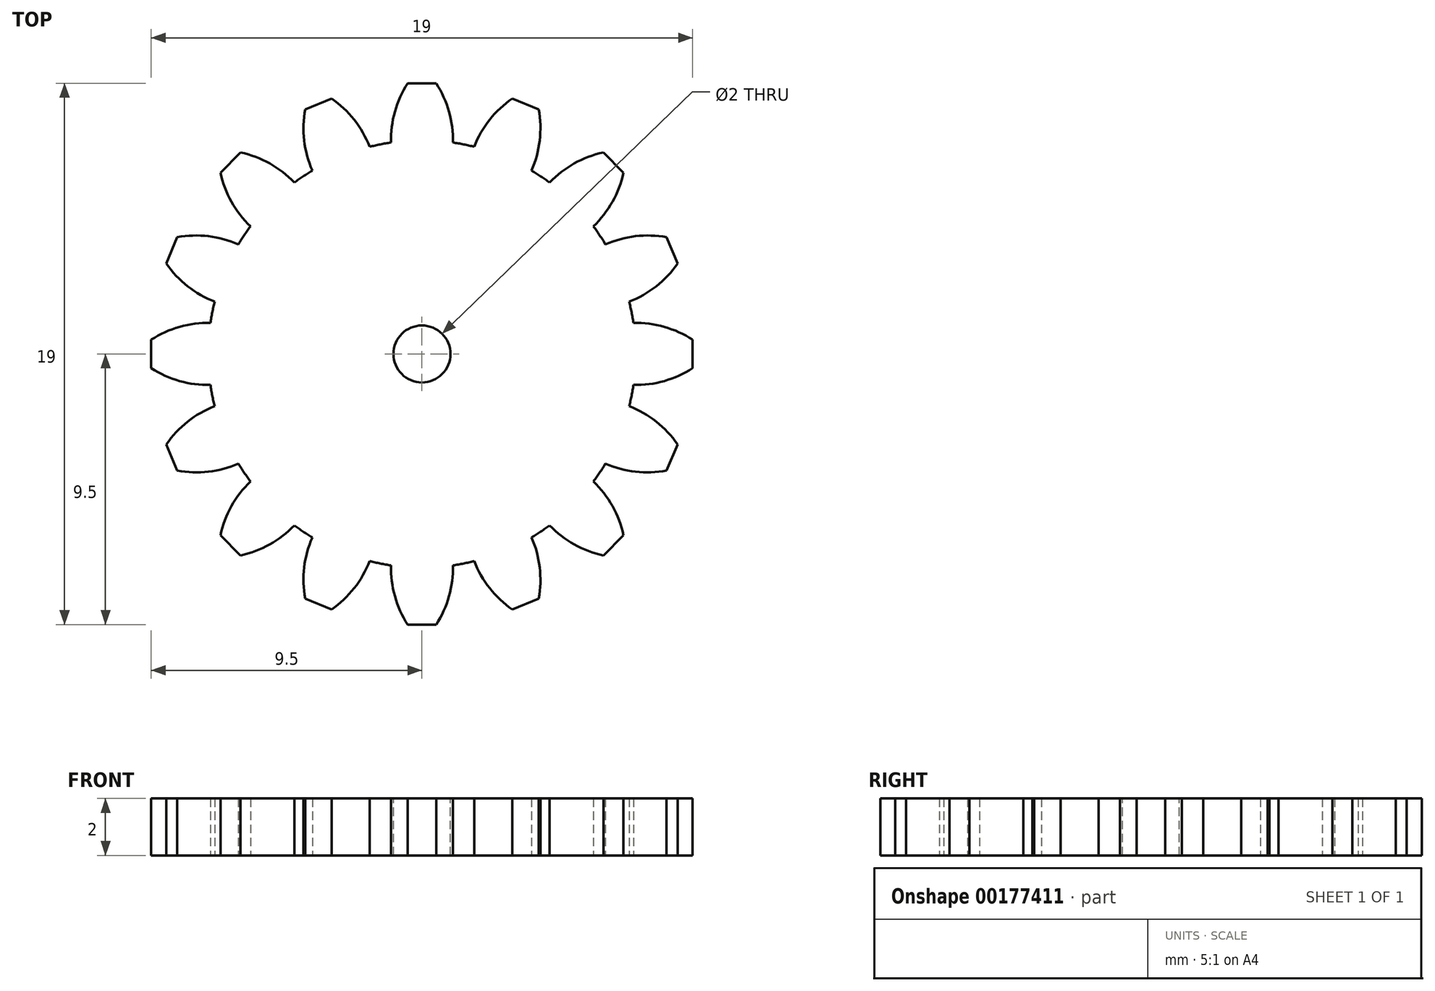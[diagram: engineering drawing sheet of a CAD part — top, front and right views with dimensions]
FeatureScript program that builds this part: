
annotation { "Feature Type Name" : "Feature", "Feature Type Description" : "" }
export const myFeature = defineFeature(function(context is Context, id is Id, definition is map)
    precondition{}
    {
        {
            var Q0;
            Q0=qCreatedBy(makeId("Top.planeOp"),FACE);
            var sketch = newSketch(context, id + "F0", { "sketchPlane" : qUnion([Q0])});
            skCircle(sketch, "E0", {"center": v(0, 0) * mm, "radius": 7.5 * mm});
            skLineSegment(sketch, "E1", {"start": v(0, 0) * mm, "end": v(0, 7.5) * mm, "construction": true});
            skLineSegment(sketch, "E2", {"start": v(0, 9.5) * mm, "end": v(-0.5, 9.5) * mm});
            skArc(sketch, "E3", {"start": v(-0.5, 9.5) * mm, "mid": v(-0.95, 8.5) * mm, "end": v(-1.09, 7.42) * mm});
            skLineSegment(sketch, "E4.MirrorCS", {"start": v(0, 9.5) * mm, "end": v(0.5, 9.5) * mm});
            skArc(sketch, "E5.MirrorCS", {"start": v(0.5, 9.5) * mm, "mid": v(0.95, 8.5) * mm, "end": v(1.09, 7.42) * mm});
            skArc(sketch, "E6.1.0", {"start": v(-4.1, 8.59) * mm, "mid": v(-4.13, 7.5) * mm, "end": v(-3.85, 6.44) * mm});
            skLineSegment(sketch, "E6.1.1", {"start": v(-3.64, 8.78) * mm, "end": v(-4.1, 8.59) * mm});
            skLineSegment(sketch, "E6.1.2", {"start": v(-3.64, 8.78) * mm, "end": v(-3.17, 8.97) * mm});
            skArc(sketch, "E6.1.3", {"start": v(-3.17, 8.97) * mm, "mid": v(-2.38, 8.22) * mm, "end": v(-1.83, 7.27) * mm});
            skArc(sketch, "E6.2.0", {"start": v(-7.07, 6.36) * mm, "mid": v(-6.69, 5.34) * mm, "end": v(-6.02, 4.48) * mm});
            skLineSegment(sketch, "E6.2.1", {"start": v(-6.72, 6.72) * mm, "end": v(-7.07, 6.36) * mm});
            skLineSegment(sketch, "E6.2.2", {"start": v(-6.72, 6.72) * mm, "end": v(-6.36, 7.07) * mm});
            skArc(sketch, "E6.2.3", {"start": v(-6.36, 7.07) * mm, "mid": v(-5.34, 6.69) * mm, "end": v(-4.48, 6.02) * mm});
            skArc(sketch, "E6.3.0", {"start": v(-8.97, 3.17) * mm, "mid": v(-8.22, 2.38) * mm, "end": v(-7.27, 1.83) * mm});
            skLineSegment(sketch, "E6.3.1", {"start": v(-8.78, 3.64) * mm, "end": v(-8.97, 3.17) * mm});
            skLineSegment(sketch, "E6.3.2", {"start": v(-8.78, 3.64) * mm, "end": v(-8.59, 4.1) * mm});
            skArc(sketch, "E6.3.3", {"start": v(-8.59, 4.1) * mm, "mid": v(-7.5, 4.13) * mm, "end": v(-6.44, 3.85) * mm});
            skArc(sketch, "E6.4.0", {"start": v(-9.5, -0.5) * mm, "mid": v(-8.5, -0.95) * mm, "end": v(-7.42, -1.09) * mm});
            skLineSegment(sketch, "E6.4.1", {"start": v(-9.5, 0) * mm, "end": v(-9.5, -0.5) * mm});
            skLineSegment(sketch, "E6.4.2", {"start": v(-9.5, 0) * mm, "end": v(-9.5, 0.5) * mm});
            skArc(sketch, "E6.4.3", {"start": v(-9.5, 0.5) * mm, "mid": v(-8.5, 0.95) * mm, "end": v(-7.42, 1.09) * mm});
            skArc(sketch, "E6.5.0", {"start": v(-8.59, -4.1) * mm, "mid": v(-7.5, -4.13) * mm, "end": v(-6.44, -3.85) * mm});
            skLineSegment(sketch, "E6.5.1", {"start": v(-8.78, -3.64) * mm, "end": v(-8.59, -4.1) * mm});
            skLineSegment(sketch, "E6.5.2", {"start": v(-8.78, -3.64) * mm, "end": v(-8.97, -3.17) * mm});
            skArc(sketch, "E6.5.3", {"start": v(-8.97, -3.17) * mm, "mid": v(-8.22, -2.38) * mm, "end": v(-7.27, -1.83) * mm});
            skArc(sketch, "E6.6.0", {"start": v(-6.36, -7.07) * mm, "mid": v(-5.34, -6.69) * mm, "end": v(-4.48, -6.02) * mm});
            skLineSegment(sketch, "E6.6.1", {"start": v(-6.72, -6.72) * mm, "end": v(-6.36, -7.07) * mm});
            skLineSegment(sketch, "E6.6.2", {"start": v(-6.72, -6.72) * mm, "end": v(-7.07, -6.36) * mm});
            skArc(sketch, "E6.6.3", {"start": v(-7.07, -6.36) * mm, "mid": v(-6.69, -5.34) * mm, "end": v(-6.02, -4.48) * mm});
            skArc(sketch, "E6.7.0", {"start": v(-3.17, -8.97) * mm, "mid": v(-2.38, -8.22) * mm, "end": v(-1.83, -7.27) * mm});
            skLineSegment(sketch, "E6.7.1", {"start": v(-3.64, -8.78) * mm, "end": v(-3.17, -8.97) * mm});
            skLineSegment(sketch, "E6.7.2", {"start": v(-3.64, -8.78) * mm, "end": v(-4.1, -8.59) * mm});
            skArc(sketch, "E6.7.3", {"start": v(-4.1, -8.59) * mm, "mid": v(-4.13, -7.5) * mm, "end": v(-3.85, -6.44) * mm});
            skArc(sketch, "E6.8.0", {"start": v(0.5, -9.5) * mm, "mid": v(0.95, -8.5) * mm, "end": v(1.09, -7.42) * mm});
            skLineSegment(sketch, "E6.8.1", {"start": v(0, -9.5) * mm, "end": v(0.5, -9.5) * mm});
            skLineSegment(sketch, "E6.8.2", {"start": v(0, -9.5) * mm, "end": v(-0.5, -9.5) * mm});
            skArc(sketch, "E6.8.3", {"start": v(-0.5, -9.5) * mm, "mid": v(-0.95, -8.5) * mm, "end": v(-1.09, -7.42) * mm});
            skArc(sketch, "E6.9.0", {"start": v(4.1, -8.59) * mm, "mid": v(4.13, -7.5) * mm, "end": v(3.85, -6.44) * mm});
            skLineSegment(sketch, "E6.9.1", {"start": v(3.64, -8.78) * mm, "end": v(4.1, -8.59) * mm});
            skLineSegment(sketch, "E6.9.2", {"start": v(3.64, -8.78) * mm, "end": v(3.17, -8.97) * mm});
            skArc(sketch, "E6.9.3", {"start": v(3.17, -8.97) * mm, "mid": v(2.38, -8.22) * mm, "end": v(1.83, -7.27) * mm});
            skArc(sketch, "E6.10.0", {"start": v(7.07, -6.36) * mm, "mid": v(6.69, -5.34) * mm, "end": v(6.02, -4.48) * mm});
            skLineSegment(sketch, "E6.10.1", {"start": v(6.72, -6.72) * mm, "end": v(7.07, -6.36) * mm});
            skLineSegment(sketch, "E6.10.2", {"start": v(6.72, -6.72) * mm, "end": v(6.36, -7.07) * mm});
            skArc(sketch, "E6.10.3", {"start": v(6.36, -7.07) * mm, "mid": v(5.34, -6.69) * mm, "end": v(4.48, -6.02) * mm});
            skArc(sketch, "E6.11.0", {"start": v(8.97, -3.17) * mm, "mid": v(8.22, -2.38) * mm, "end": v(7.27, -1.83) * mm});
            skLineSegment(sketch, "E6.11.1", {"start": v(8.78, -3.64) * mm, "end": v(8.97, -3.17) * mm});
            skLineSegment(sketch, "E6.11.2", {"start": v(8.78, -3.64) * mm, "end": v(8.59, -4.1) * mm});
            skArc(sketch, "E6.11.3", {"start": v(8.59, -4.1) * mm, "mid": v(7.5, -4.13) * mm, "end": v(6.44, -3.85) * mm});
            skArc(sketch, "E6.12.0", {"start": v(9.5, 0.5) * mm, "mid": v(8.5, 0.95) * mm, "end": v(7.42, 1.09) * mm});
            skLineSegment(sketch, "E6.12.1", {"start": v(9.5, 0) * mm, "end": v(9.5, 0.5) * mm});
            skLineSegment(sketch, "E6.12.2", {"start": v(9.5, 0) * mm, "end": v(9.5, -0.5) * mm});
            skArc(sketch, "E6.12.3", {"start": v(9.5, -0.5) * mm, "mid": v(8.5, -0.95) * mm, "end": v(7.42, -1.09) * mm});
            skArc(sketch, "E6.13.0", {"start": v(8.59, 4.1) * mm, "mid": v(7.5, 4.13) * mm, "end": v(6.44, 3.85) * mm});
            skLineSegment(sketch, "E6.13.1", {"start": v(8.78, 3.64) * mm, "end": v(8.59, 4.1) * mm});
            skLineSegment(sketch, "E6.13.2", {"start": v(8.78, 3.64) * mm, "end": v(8.97, 3.17) * mm});
            skArc(sketch, "E6.13.3", {"start": v(8.97, 3.17) * mm, "mid": v(8.22, 2.38) * mm, "end": v(7.27, 1.83) * mm});
            skArc(sketch, "E6.14.0", {"start": v(6.36, 7.07) * mm, "mid": v(5.34, 6.69) * mm, "end": v(4.48, 6.02) * mm});
            skLineSegment(sketch, "E6.14.1", {"start": v(6.72, 6.72) * mm, "end": v(6.36, 7.07) * mm});
            skLineSegment(sketch, "E6.14.2", {"start": v(6.72, 6.72) * mm, "end": v(7.07, 6.36) * mm});
            skArc(sketch, "E6.14.3", {"start": v(7.07, 6.36) * mm, "mid": v(6.69, 5.34) * mm, "end": v(6.02, 4.48) * mm});
            skArc(sketch, "E6.15.0", {"start": v(3.17, 8.97) * mm, "mid": v(2.38, 8.22) * mm, "end": v(1.83, 7.27) * mm});
            skLineSegment(sketch, "E6.15.1", {"start": v(3.64, 8.78) * mm, "end": v(3.17, 8.97) * mm});
            skLineSegment(sketch, "E6.15.2", {"start": v(3.64, 8.78) * mm, "end": v(4.1, 8.59) * mm});
            skArc(sketch, "E6.15.3", {"start": v(4.1, 8.59) * mm, "mid": v(4.13, 7.5) * mm, "end": v(3.85, 6.44) * mm});
            skSolve(sketch);
        }
        {
            var Q0;
            Q0 = qSketchRegion(id + "F0", true);
            extrude(context, id + "F1", {"entities" : qUnion([Q0]), "depth" : 2 * mm});
        }
        {
            var Q0;
            Q0=makeQuery(id+"F1.opExtrude","CAP_FACE",FACE,{"disambiguationData":[OSD([sQuery(id+"F0.wireOp",EDGE,"E0"),sQuery(id+"F0.wireOp",EDGE,"E2"),sQuery(id+"F0.wireOp",EDGE,"E3"),sQuery(id+"F0.wireOp",EDGE,"E4.MirrorCS"),sQuery(id+"F0.wireOp",EDGE,"E5.MirrorCS"),sQuery(id+"F0.wireOp",EDGE,"E6.1.0"),sQuery(id+"F0.wireOp",EDGE,"E6.1.1"),sQuery(id+"F0.wireOp",EDGE,"E6.1.2"),sQuery(id+"F0.wireOp",EDGE,"E6.1.3"),sQuery(id+"F0.wireOp",EDGE,"E6.2.0"),sQuery(id+"F0.wireOp",EDGE,"E6.2.1"),sQuery(id+"F0.wireOp",EDGE,"E6.2.2"),sQuery(id+"F0.wireOp",EDGE,"E6.2.3"),sQuery(id+"F0.wireOp",EDGE,"E6.3.0"),sQuery(id+"F0.wireOp",EDGE,"E6.3.1"),sQuery(id+"F0.wireOp",EDGE,"E6.3.2"),sQuery(id+"F0.wireOp",EDGE,"E6.3.3"),sQuery(id+"F0.wireOp",EDGE,"E6.4.0"),sQuery(id+"F0.wireOp",EDGE,"E6.4.1"),sQuery(id+"F0.wireOp",EDGE,"E6.4.2"),sQuery(id+"F0.wireOp",EDGE,"E6.4.3"),sQuery(id+"F0.wireOp",EDGE,"E6.5.0"),sQuery(id+"F0.wireOp",EDGE,"E6.5.1"),sQuery(id+"F0.wireOp",EDGE,"E6.5.2"),sQuery(id+"F0.wireOp",EDGE,"E6.5.3"),sQuery(id+"F0.wireOp",EDGE,"E6.6.0"),sQuery(id+"F0.wireOp",EDGE,"E6.6.1"),sQuery(id+"F0.wireOp",EDGE,"E6.6.2"),sQuery(id+"F0.wireOp",EDGE,"E6.6.3"),sQuery(id+"F0.wireOp",EDGE,"E6.7.0"),sQuery(id+"F0.wireOp",EDGE,"E6.7.1"),sQuery(id+"F0.wireOp",EDGE,"E6.7.2"),sQuery(id+"F0.wireOp",EDGE,"E6.7.3"),sQuery(id+"F0.wireOp",EDGE,"E6.8.0"),sQuery(id+"F0.wireOp",EDGE,"E6.8.1"),sQuery(id+"F0.wireOp",EDGE,"E6.8.2"),sQuery(id+"F0.wireOp",EDGE,"E6.8.3"),sQuery(id+"F0.wireOp",EDGE,"E6.9.0"),sQuery(id+"F0.wireOp",EDGE,"E6.9.1"),sQuery(id+"F0.wireOp",EDGE,"E6.9.2"),sQuery(id+"F0.wireOp",EDGE,"E6.9.3"),sQuery(id+"F0.wireOp",EDGE,"E6.10.0"),sQuery(id+"F0.wireOp",EDGE,"E6.10.1"),sQuery(id+"F0.wireOp",EDGE,"E6.10.2"),sQuery(id+"F0.wireOp",EDGE,"E6.10.3"),sQuery(id+"F0.wireOp",EDGE,"E6.11.0"),sQuery(id+"F0.wireOp",EDGE,"E6.11.1"),sQuery(id+"F0.wireOp",EDGE,"E6.11.2"),sQuery(id+"F0.wireOp",EDGE,"E6.11.3"),sQuery(id+"F0.wireOp",EDGE,"E6.12.0"),sQuery(id+"F0.wireOp",EDGE,"E6.12.1"),sQuery(id+"F0.wireOp",EDGE,"E6.12.2"),sQuery(id+"F0.wireOp",EDGE,"E6.12.3"),sQuery(id+"F0.wireOp",EDGE,"E6.13.0"),sQuery(id+"F0.wireOp",EDGE,"E6.13.1"),sQuery(id+"F0.wireOp",EDGE,"E6.13.2"),sQuery(id+"F0.wireOp",EDGE,"E6.13.3"),sQuery(id+"F0.wireOp",EDGE,"E6.14.0"),sQuery(id+"F0.wireOp",EDGE,"E6.14.1"),sQuery(id+"F0.wireOp",EDGE,"E6.14.2"),sQuery(id+"F0.wireOp",EDGE,"E6.14.3"),sQuery(id+"F0.wireOp",EDGE,"E6.15.0"),sQuery(id+"F0.wireOp",EDGE,"E6.15.1"),sQuery(id+"F0.wireOp",EDGE,"E6.15.2"),sQuery(id+"F0.wireOp",EDGE,"E6.15.3")])],"isStart":false});
            var sketch = newSketch(context, id + "F2", { "sketchPlane" : qUnion([Q0])});
            skCircle(sketch, "E7", {"center": v(0, 0) * mm, "radius": 1 * mm});
            skSolve(sketch);
        }
        {
            var Q0;
            Q0 = qSketchRegion(id + "F2", true);
            extrude(context, id + "F3", {"entities" : qUnion([Q0]), "operationType" : NewBodyOperationType.REMOVE, "endBound" : BoundingType.THROUGH_ALL, "oppositeDirection" : true, "depth" : 25 * mm});
        }
    });
